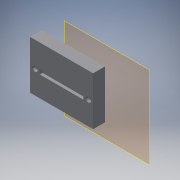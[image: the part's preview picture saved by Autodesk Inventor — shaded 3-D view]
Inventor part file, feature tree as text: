
AUTODESK INVENTOR PART (.ipt)
format: ipt  version: 2016 (Build 200138000, 138)  size: 117,760 bytes
history: native  units: in
note: dims shown in document units (in); Inventor stores cm internally (conversion verified against a paired STEP export)
features: extrude x3, sketch x3, plane x1, projected_geometry x1
ambient origin geometry x8: Origin, YZ Plane, XZ Plane, XY Plane, X Axis, Y Axis, Z Axis, Center Point
bodies: Solid1 (feature_tree)
feature tree (8):
  plane  "Work Plane1"
  extrude  "Extrusion1"  Depth=1.7717in
  extrude  "Extrusion2"  Depth=0.2756in
  extrude  "Extrusion3"  Depth=0.0787in
  sketch  "Sketch1"  dims[d0=1.3583in d1=1.7717in]
  sketch  "Sketch2"  dims[d2=0.3346in d3=0.0in d4=0.2756in]
  sketch  "Sketch3"  dims[d5=1.2205in d6=0.0984in d7=0.0984in d8=0.0787in d9=0.0in d11=0.138in d12=0.138in d13=0.0787in d14=0.0in]
  projected_geometry  "Projected Loop1"
